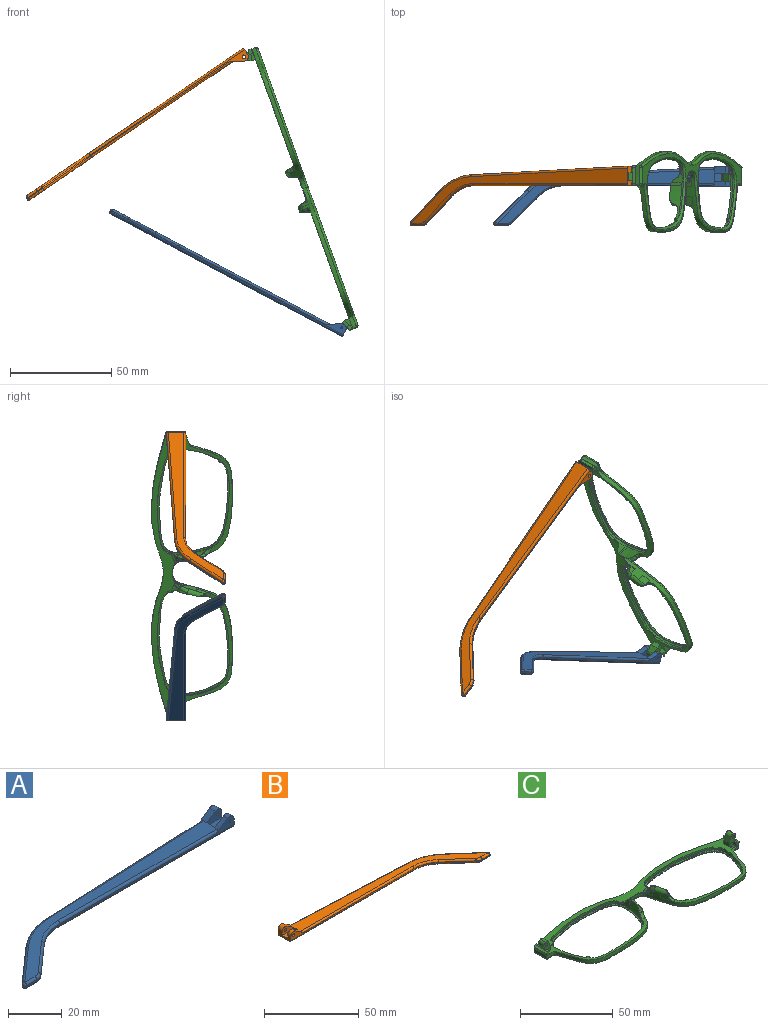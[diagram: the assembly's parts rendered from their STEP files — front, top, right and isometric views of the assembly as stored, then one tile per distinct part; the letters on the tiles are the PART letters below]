
ASSEMBLY  parts=3 mates=2
PART A: 43 faces, bbox 130.2x29.5x5.9 mm
  f0: plane 9.62x3.72mm, normal (1,0,0), area 24.7mm2, adj f1,f3,f4,f5,f10,f16,f18,f28
  f1: cylinder r=2.2mm len=3.45mm, axis (0,-1,0), area 11mm2, adj f0,f2,f4,f37
  f2: plane 6.01x3.91mm, normal (-0.55,0,0.84), area 12.7mm2, adj f1,f4,f9,f19,f37
  f3: plane 2.26x0.1mm, normal (0,0,1), area 0.1mm2, adj f0,f5,f18
  f4: plane 92.1x4.9mm, normal (0,-1,0), area 79.9mm2, adj f0,f1,f2,f14,f19,f36,f42
  f5: plane 93.42x4.13mm, normal (-0.04,1,0), area 64.8mm2, adj f0,f3,f11,f15,f17,f27,f28
  f6: plane 17.82x15.72mm, normal (-0.66,0.75,0), area 14.3mm2, adj f11,f12,f25,f30
  f7: plane 5.46x0.6mm, normal (0,-1,0), area 3.3mm2, adj f12,f13,f23,f32
  f8: plane 14.99x13.23mm, normal (0.66,-0.75,0), area 12mm2, adj f13,f14,f21,f34
  f9: plane 121.18x26.73mm, normal (0,0,1), area 627.7mm2, adj f2,f17,f19,f20,f21,f22,f23,f25
  f10: plane 129.1x27.08mm, normal (0,0,-1), area 686.5mm2, adj f0,f28,f29,f30,f32,f33,f34,f35
  f11: cylinder r=30mm len=18.52mm, axis (0,0,-1), area 12.2mm2, adj f5,f6,f26,f29
  f12: cylinder r=1mm len=1.75mm, axis (0,0,-1), area 1.5mm2, adj f6,f7,f24,f31
  f13: cylinder r=5mm len=3.31mm, axis (0,0,-1), area 2.2mm2, adj f7,f8,f22,f33
  f14: cylinder r=20mm len=13.23mm, axis (0,0,1), area 8.7mm2, adj f4,f8,f20,f35
  f15: plane 5.66x0.25mm, normal (0,0,-1), area 0.7mm2, adj f5,f17,f18
  f16: cylinder r=2.2mm len=3.45mm, axis (0,-1,0), area 14.8mm2, adj f0,f17,f18,f38
  f17: plane 6.01x3.91mm, normal (-0.55,0,0.84), area 16.9mm2, adj f5,f9,f15,f16,f18,f27,f38
  f18: plane 7.92x3.3mm, normal (0,1,0), area 15.9mm2, adj f0,f3,f15,f16,f17,f41
  f19: cylinder r=1mm len=84.18mm, axis (-1,0,0), area 131.4mm2, adj f2,f4,f9,f20
  f20: torus R=21mm, axis (0,0,1), area 23.1mm2, adj f9,f14,f19,f21
  f21: cylinder r=1mm len=15.65mm, axis (-0.75,-0.66,0), area 31.4mm2, adj f8,f9,f20,f22
  f22: torus R=4mm, axis (0,0,1), area 5.3mm2, adj f9,f13,f21,f23
  f23: cylinder r=1mm len=5.46mm, axis (-1,0,0), area 8.6mm2, adj f7,f9,f22,f24
  f24: sphere r=1mm, area 2.4mm2, adj f12,f23,f25
  f25: cylinder r=1mm len=18.48mm, axis (0.75,0.66,0), area 37.3mm2, adj f6,f9,f24,f26
  f26: torus R=29mm, axis (0,0,1), area 31.6mm2, adj f9,f11,f25,f27
  f27: cylinder r=1mm len=85.5mm, axis (1,0.04,0), area 133.5mm2, adj f5,f9,f17,f26
  f28: cylinder r=1mm len=93.46mm, axis (-1,-0.04,0), area 146.9mm2, adj f0,f5,f10,f29
  f29: torus R=29mm, axis (0,0,1), area 31.6mm2, adj f10,f11,f28,f30
  f30: cylinder r=1mm len=18.48mm, axis (-0.75,-0.66,0), area 37.3mm2, adj f6,f10,f29,f31
  f31: sphere r=1mm, area 2.4mm2, adj f12,f30,f32
  f32: cylinder r=1mm len=5.46mm, axis (1,0,0), area 8.6mm2, adj f7,f10,f31,f33
  f33: torus R=4mm, axis (0,0,1), area 5.3mm2, adj f10,f13,f32,f34
  f34: cylinder r=1mm len=15.65mm, axis (0.75,0.66,0), area 31.4mm2, adj f8,f10,f33,f35
  f35: torus R=21mm, axis (0,0,1), area 23.1mm2, adj f10,f14,f34,f36
  f36: cylinder r=1mm len=92.1mm, axis (1,0,0), area 144.7mm2, adj f0,f4,f10,f35
  f37: plane 7.92x4.7mm, normal (0,1,0), area 27mm2, adj f0,f1,f2,f39,f40,f42
  f38: plane 7.92x4.7mm, normal (0,-1,0), area 27mm2, adj f0,f16,f17,f39,f40,f41
  f39: plane 7.92x4.1mm, normal (0,0,1), area 32.5mm2, adj f0,f37,f38,f40
  f40: plane 4.1x1.4mm, normal (1,0,0), area 5.7mm2, adj f9,f37,f38,f39
  f41: cylinder r=0.5mm len=3.1mm, axis (0,-1,0), area 9.7mm2, adj f18,f38
  f42: cylinder r=0.5mm len=2.3mm, axis (0,-1,0), area 7.2mm2, adj f4,f37
PART B: 43 faces, bbox 130.2x29.5x5.9 mm
  f0: plane 9.62x3.72mm, normal (-1,0,0), area 24.7mm2, adj f1,f3,f4,f5,f10,f16,f18,f28
  f1: cylinder r=2.2mm len=3.45mm, axis (0,-1,0), area 11mm2, adj f0,f2,f4,f37
  f2: plane 6.01x3.91mm, normal (0.55,0,0.84), area 12.7mm2, adj f1,f4,f9,f19,f37
  f3: plane 2.26x0.1mm, normal (0,0,1), area 0.1mm2, adj f0,f5,f18
  f4: plane 92.1x4.9mm, normal (0,-1,0), area 78.2mm2, adj f0,f1,f2,f14,f19,f36,f42
  f5: plane 93.42x4.13mm, normal (0.04,1,0), area 64.8mm2, adj f0,f3,f11,f15,f17,f27,f28
  f6: plane 17.82x15.72mm, normal (0.66,0.75,0), area 14.3mm2, adj f11,f12,f25,f30
  f7: plane 5.46x0.6mm, normal (0,-1,0), area 3.3mm2, adj f12,f13,f23,f32
  f8: plane 14.99x13.23mm, normal (-0.66,-0.75,0), area 12mm2, adj f13,f14,f21,f34
  f9: plane 121.18x26.73mm, normal (0,0,1), area 627.7mm2, adj f2,f17,f19,f20,f21,f22,f23,f25
  f10: plane 129.1x27.08mm, normal (0,0,-1), area 686.5mm2, adj f0,f28,f29,f30,f32,f33,f34,f35
  f11: cylinder r=30mm len=18.52mm, axis (0,0,-1), area 12.2mm2, adj f5,f6,f26,f29
  f12: cylinder r=1mm len=1.75mm, axis (0,0,-1), area 1.5mm2, adj f6,f7,f24,f31
  f13: cylinder r=5mm len=3.31mm, axis (0,0,-1), area 2.2mm2, adj f7,f8,f22,f33
  f14: cylinder r=20mm len=13.23mm, axis (0,0,1), area 8.7mm2, adj f4,f8,f20,f35
  f15: plane 5.66x0.25mm, normal (0,0,-1), area 0.7mm2, adj f5,f17,f18
  f16: cylinder r=2.2mm len=3.45mm, axis (0,-1,0), area 14.8mm2, adj f0,f17,f18,f38
  f17: plane 6.01x3.91mm, normal (0.55,0,0.84), area 16.9mm2, adj f5,f9,f15,f16,f18,f27,f38
  f18: plane 7.92x3.3mm, normal (0,1,0), area 14.3mm2, adj f0,f3,f15,f16,f17,f41
  f19: cylinder r=1mm len=84.18mm, axis (1,0,0), area 131.4mm2, adj f2,f4,f9,f20
  f20: torus R=21mm, axis (0,0,1), area 23.1mm2, adj f9,f14,f19,f21
  f21: cylinder r=1mm len=15.65mm, axis (0.75,-0.66,0), area 31.4mm2, adj f8,f9,f20,f22
  f22: torus R=4mm, axis (0,0,1), area 5.3mm2, adj f9,f13,f21,f23
  f23: cylinder r=1mm len=5.46mm, axis (1,0,0), area 8.6mm2, adj f7,f9,f22,f24
  f24: sphere r=1mm, area 2.4mm2, adj f12,f23,f25
  f25: cylinder r=1mm len=18.48mm, axis (-0.75,0.66,0), area 37.3mm2, adj f6,f9,f24,f26
  f26: torus R=29mm, axis (0,0,1), area 31.6mm2, adj f9,f11,f25,f27
  f27: cylinder r=1mm len=85.5mm, axis (-1,0.04,0), area 133.5mm2, adj f5,f9,f17,f26
  f28: cylinder r=1mm len=93.46mm, axis (1,-0.04,0), area 146.9mm2, adj f0,f5,f10,f29
  f29: torus R=29mm, axis (0,0,1), area 31.6mm2, adj f10,f11,f28,f30
  f30: cylinder r=1mm len=18.48mm, axis (0.75,-0.66,0), area 37.3mm2, adj f6,f10,f29,f31
  f31: sphere r=1mm, area 2.4mm2, adj f12,f30,f32
  f32: cylinder r=1mm len=5.46mm, axis (-1,0,0), area 8.6mm2, adj f7,f10,f31,f33
  f33: torus R=4mm, axis (0,0,1), area 5.3mm2, adj f10,f13,f32,f34
  f34: cylinder r=1mm len=15.65mm, axis (-0.75,0.66,0), area 31.4mm2, adj f8,f10,f33,f35
  f35: torus R=21mm, axis (0,0,1), area 23.1mm2, adj f10,f14,f34,f36
  f36: cylinder r=1mm len=92.1mm, axis (-1,0,0), area 144.7mm2, adj f0,f4,f10,f35
  f37: plane 7.92x4.7mm, normal (0,1,0), area 25.4mm2, adj f0,f1,f2,f39,f40,f42
  f38: plane 7.92x4.7mm, normal (0,-1,0), area 25.4mm2, adj f0,f16,f17,f39,f40,f41
  f39: plane 7.92x4.1mm, normal (0,0,1), area 32.5mm2, adj f0,f37,f38,f40
  f40: plane 4.1x1.4mm, normal (-1,0,0), area 5.7mm2, adj f9,f37,f38,f39
  f41: cylinder r=0.88mm len=3.1mm, axis (0,-1,0), area 17mm2, adj f18,f38
  f42: cylinder r=0.88mm len=2.3mm, axis (0,-1,0), area 12.6mm2, adj f4,f37
PART C: 118 faces, bbox 148.1x40.9x17.9 mm
  f0: bspline ~1.82x1.22mm, area 0.7mm2, adj f2,f7,f37,f52
  f1: plane 147.69x40.46mm, normal (0,0,1), area 858.2mm2, adj f4,f5,f6,f7,f8,f12,f20,f23
  f2: bspline ~6.1x4.93mm, area 12.7mm2, adj f0,f7,f37,f41,f43,f52,f53
  f3: plane 4.46x1.45mm, normal (0,0,1), area 0.1mm2, adj f7,f38
  f4: plane 1.23x0.04mm, normal (0,0,1), area 0mm2, adj f1,f7,f22
  f5: plane 6.97x5.07mm, normal (0,1,0), area 22.7mm2, adj f1,f20,f21,f25,f27,f28,f30,f31
  f6: plane 3.2x2.36mm, normal (0,-1,0), area 5.7mm2, adj f1,f20,f26,f29
  f7: extruded ~73.26x39.84mm, area 292.7mm2, adj f0,f1,f2,f3,f4,f8,f13,f14
  f8: extruded ~35.39x5.69mm, area 72.2mm2, adj f1,f7,f18,f67
  f9: plane 144.78x37.85mm, normal (0,0,-1), area 582.4mm2, adj f13,f15,f17,f18,f19,f71,f73,f75
  f10: plane 56.06x35.45mm, normal (0,0,1), area 127mm2, adj f11,f19
  f11: extruded ~55.69x35.36mm, area 160.5mm2, adj f10,f12
  f12: extruded ~55.69x35.36mm, area 226.3mm2, adj f1,f11,f39,f40,f41,f42,f43,f44
  f13: bspline ~73.27x30.39mm, area 161.7mm2, adj f7,f9,f14,f71
  f14: bspline ~1x1mm, area 0.8mm2, adj f7,f13,f15
  f15: bspline ~8.99x1.23mm, area 12.6mm2, adj f7,f9,f14,f16
  f16: bspline ~1.04x1mm, area 0.7mm2, adj f7,f15,f17
  f17: bspline ~45.86x8.59mm, area 59.8mm2, adj f7,f9,f16,f18
  f18: bspline ~37.01x6.7mm, area 56.6mm2, adj f8,f9,f17,f76
  f19: bspline ~56.23x35.9mm, area 235.3mm2, adj f9,f10
  f20: plane 4x2.36mm, normal (-1,0,0), area 9.5mm2, adj f1,f5,f6,f21
  f21: plane 4x0.02mm, normal (0.34,0,0.94), area 0.1mm2, adj f5,f20,f28
  f22: plane 2.76x2.53mm, normal (0,-1,0), area 3.9mm2, adj f4,f26,f27,f35,f56
  f23: plane 7.67x1.6mm, normal (0.94,0,-0.34), area 13mm2, adj f1,f35,f36,f56
  f24: plane 2.1x1.69mm, normal (0,1,0), area 2.8mm2, adj f1,f25,f27,f36,f56
  f25: plane 3.3x2.1mm, normal (-1,0,0), area 6.9mm2, adj f1,f5,f24,f27
  f26: plane 2.35x2.1mm, normal (-1,0,0), area 4.9mm2, adj f1,f6,f22,f27,f29
  f27: plane 9.65x1.24mm, normal (0,0,1), area 8.2mm2, adj f5,f22,f24,f25,f26,f29,f30,f56
  f28: plane 4x3.31mm, normal (-0.94,0,0.34), area 14.1mm2, adj f5,f21,f29,f32
  f29: plane 5.77x5.06mm, normal (0,-1,0), area 17mm2, adj f6,f26,f27,f28,f30,f31,f32,f33
  f30: plane 4x2.21mm, normal (0.94,0,-0.34), area 9.4mm2, adj f5,f27,f29,f33
  f31: plane 4x0.01mm, normal (0.34,0,0.94), area 0mm2, adj f5,f29,f32,f33
  f32: cylinder r=1.98mm len=4mm, axis (0,1,0), area 12.4mm2, adj f5,f28,f29,f31
  f33: cylinder r=1.98mm len=4mm, axis (0,-1,0), area 12.4mm2, adj f5,f29,f30,f31
  f34: cylinder r=0.88mm len=4mm, axis (0,-1,0), area 22mm2, adj f5,f29
  f35: cone r=1mm half-angle=20deg, axis (0,0,1), area 2.3mm2, adj f1,f22,f23,f56
  f36: cylinder r=1mm len=2.28mm, axis (-0.34,0,-0.94), area 3mm2, adj f1,f23,f24,f56
  f37: extruded ~3.67x3.11mm, area 5.9mm2, adj f0,f2,f7,f59
  f38: extruded ~4.44x3.32mm, area 15.1mm2, adj f3,f7,f42,f43,f55
  f39: extruded ~4.98x1.37mm, area 6.6mm2, adj f12,f41
  f40: plane 3.63x0.97mm, normal (0,0,1), area 0.3mm2, adj f12,f41,f43
  f41: bspline ~15.5x15.35mm, area 6.4mm2, adj f2,f12,f39,f40,f54
  f42: bspline ~7.26x7.26mm, area 6.3mm2, adj f12,f38,f43,f55
  f43: bspline ~10.29x4.84mm, area 21.4mm2, adj f2,f7,f12,f38,f40,f42
  f44: plane 3.19x1.37mm, normal (0,0,-1), area 2.1mm2, adj f12,f45
  f45: cylinder r=2.28mm len=3.17mm, axis (0,0,1), area 2.1mm2, adj f1,f12,f44,f54
  f46: plane 3.14x2.79mm, normal (0,0,-1), area 3.9mm2, adj f12,f47
  f47: cylinder r=2.28mm len=3.13mm, axis (0,0,1), area 2.5mm2, adj f1,f12,f46
  f48: plane 1.79x1.31mm, normal (0,0,-1), area 0.9mm2, adj f12,f49
  f49: cylinder r=1.3mm len=1.78mm, axis (0,0,1), area 1.3mm2, adj f1,f12,f48
  f50: plane 1.95x1.68mm, normal (0,0,-1), area 1.5mm2, adj f12,f51
  f51: cylinder r=1.3mm len=1.93mm, axis (0,0,1), area 1.5mm2, adj f1,f12,f50
  f52: bspline ~2.66x2.04mm, area 1.9mm2, adj f0,f2,f7,f53,f58
  f53: bspline ~3.55x3.47mm, area 3.7mm2, adj f1,f2,f52,f54,f58
  f54: bspline ~6.16x4.45mm, area 7.9mm2, adj f1,f12,f41,f45,f53
  f55: bspline ~3.7x3.66mm, area 7.8mm2, adj f1,f7,f12,f38,f42
  f56: plane 9.71x1.44mm, normal (0.34,0,0.94), area 13.9mm2, adj f22,f23,f24,f27,f35,f36
  f57: bspline ~6.38x2.14mm, area 2.6mm2, adj f1,f7,f58,f115
  f58: bspline ~2.1x1.46mm, area 0.6mm2, adj f7,f52,f53,f57
  f59: bspline ~5.24x1.75mm, area 0mm2, adj f7,f37
  f60: bspline ~2.19x1.4mm, area 0.7mm2, adj f61,f66,f95,f110
  f61: bspline ~6.1x4.93mm, area 12.6mm2, adj f60,f66,f95,f99,f101,f110,f111
  f62: plane 4.46x1.45mm, normal (0,0,1), area 0.1mm2, adj f66,f96
  f63: plane 1.23x0.04mm, normal (0,0,1), area 0mm2, adj f1,f66,f80
  f64: plane 6.97x5.07mm, normal (0,1,0), area 22.7mm2, adj f1,f78,f79,f83,f85,f86,f88,f89
  f65: plane 3.2x2.36mm, normal (0,-1,0), area 5.7mm2, adj f1,f78,f84,f87
  f66: extruded ~73.26x39.84mm, area 292.7mm2, adj f1,f7,f60,f61,f62,f63,f67,f71
  f67: extruded ~35.39x5.69mm, area 72.2mm2, adj f1,f8,f66,f76
  f68: plane 56.06x35.45mm, normal (0,0,1), area 127mm2, adj f69,f77
  f69: extruded ~55.69x35.36mm, area 160.5mm2, adj f68,f70
  f70: extruded ~55.69x35.36mm, area 226.4mm2, adj f1,f69,f97,f98,f99,f100,f101,f102
  f71: bspline ~73.83x30.39mm, area 161.7mm2, adj f9,f13,f66,f72
  f72: bspline ~1x1mm, area 0.8mm2, adj f66,f71,f73
  f73: bspline ~8.99x1.23mm, area 12.6mm2, adj f9,f66,f72,f74
  f74: bspline ~1.04x1mm, area 0.8mm2, adj f66,f73,f75
  f75: bspline ~45.86x8.59mm, area 59.8mm2, adj f9,f66,f74,f76
  f76: bspline ~37.01x6.7mm, area 56.6mm2, adj f9,f18,f67,f75
  f77: bspline ~56.22x35.9mm, area 235.3mm2, adj f9,f68
  f78: plane 4x2.36mm, normal (1,0,0), area 9.5mm2, adj f1,f64,f65,f79
  f79: plane 4x0.02mm, normal (-0.34,0,0.94), area 0.1mm2, adj f64,f78,f86
  f80: plane 2.76x2.53mm, normal (0,-1,0), area 3.9mm2, adj f63,f84,f85,f93,f114
  f81: plane 7.67x1.6mm, normal (-0.94,0,-0.34), area 13mm2, adj f1,f93,f94,f114
  f82: plane 2.1x1.69mm, normal (0,1,0), area 2.8mm2, adj f1,f83,f85,f94,f114
  f83: plane 3.3x2.1mm, normal (1,0,0), area 6.9mm2, adj f1,f64,f82,f85
  f84: plane 2.35x2.1mm, normal (1,0,0), area 4.9mm2, adj f1,f65,f80,f85,f87
  f85: plane 9.65x1.24mm, normal (0,0,1), area 8.2mm2, adj f64,f80,f82,f83,f84,f87,f88,f114
  f86: plane 4x3.31mm, normal (0.94,0,0.34), area 14.1mm2, adj f64,f79,f87,f90
  f87: plane 5.77x5.06mm, normal (0,-1,0), area 17mm2, adj f65,f84,f85,f86,f88,f89,f90,f91
  f88: plane 4x2.21mm, normal (-0.94,0,-0.34), area 9.4mm2, adj f64,f85,f87,f91
  f89: plane 4x0.01mm, normal (-0.34,0,0.94), area 0mm2, adj f64,f87,f90,f91
  f90: cylinder r=1.98mm len=4mm, axis (0,1,0), area 12.4mm2, adj f64,f86,f87,f89
  f91: cylinder r=1.98mm len=4mm, axis (0,-1,0), area 12.4mm2, adj f64,f87,f88,f89
  f92: cylinder r=0.88mm len=4mm, axis (0,-1,0), area 22mm2, adj f64,f87
  f93: cone r=1mm half-angle=20deg, axis (0,0,1), area 2.3mm2, adj f1,f80,f81,f114
  f94: cylinder r=1mm len=2.28mm, axis (0.34,0,-0.94), area 3mm2, adj f1,f81,f82,f114
  f95: extruded ~3.67x3.11mm, area 5.9mm2, adj f60,f61,f66,f117
  f96: extruded ~4.44x3.32mm, area 15.1mm2, adj f62,f66,f100,f101,f113
  f97: extruded ~4.98x1.36mm, area 6.6mm2, adj f70,f99
  f98: plane 3.63x0.97mm, normal (0,0,1), area 0.3mm2, adj f70,f99,f101
  f99: bspline ~15.5x15.35mm, area 6.4mm2, adj f61,f70,f97,f98,f112
  f100: bspline ~7.26x7.26mm, area 6.2mm2, adj f70,f96,f101,f113
  f101: bspline ~10.29x4.84mm, area 21.5mm2, adj f61,f66,f70,f96,f98,f100
  f102: plane 3.19x1.37mm, normal (0,0,-1), area 2.1mm2, adj f70,f103
  f103: cylinder r=2.28mm len=3.17mm, axis (0,0,1), area 2.1mm2, adj f1,f70,f102,f112
  f104: plane 3.14x2.79mm, normal (0,0,-1), area 3.9mm2, adj f70,f105
  f105: cylinder r=2.28mm len=3.13mm, axis (0,0,1), area 2.5mm2, adj f1,f70,f104
  f106: plane 1.79x1.31mm, normal (0,0,-1), area 0.9mm2, adj f70,f107
  f107: cylinder r=1.3mm len=1.78mm, axis (0,0,1), area 1.3mm2, adj f1,f70,f106
  f108: plane 1.95x1.68mm, normal (0,0,-1), area 1.5mm2, adj f70,f109
  f109: cylinder r=1.3mm len=1.93mm, axis (0,0,1), area 1.5mm2, adj f1,f70,f108
  f110: bspline ~2.65x2.03mm, area 1.9mm2, adj f60,f61,f66,f111,f116
  f111: bspline ~3.55x3.47mm, area 3.7mm2, adj f1,f61,f110,f112,f116
  f112: bspline ~5.94x4.42mm, area 7.9mm2, adj f1,f70,f99,f103,f111
  f113: bspline ~3.7x3.66mm, area 7.8mm2, adj f1,f66,f70,f96,f100
  f114: plane 9.71x1.44mm, normal (-0.34,0,0.94), area 13.9mm2, adj f80,f81,f82,f85,f93,f94
  f115: bspline ~6.38x2.14mm, area 2.6mm2, adj f1,f57,f66,f116
  f116: bspline ~2.1x1.46mm, area 0.6mm2, adj f66,f110,f111,f115
  f117: bspline ~5.24x1.75mm, area 0mm2, adj f66,f95
PLACE A rot(axis=(0,1,0),27.9deg) t=(124.31,14.51,57.23)mm
PLACE B rot(axis=(0,1,0),145.7deg) t=(181.36,14.51,205.32)mm
PLACE C rot(axis=(0,-1,0),109.8deg) t=(161.2,19.12,101.74)mm
MATE revolute A.f1 <-> C.f90  axis (0,-1,0) through (178.74,22.97,32.54)mm
MATE revolute B.f41 <-> C.f33  axis (0,-1,0) through (130.52,22.97,166.2)mm
